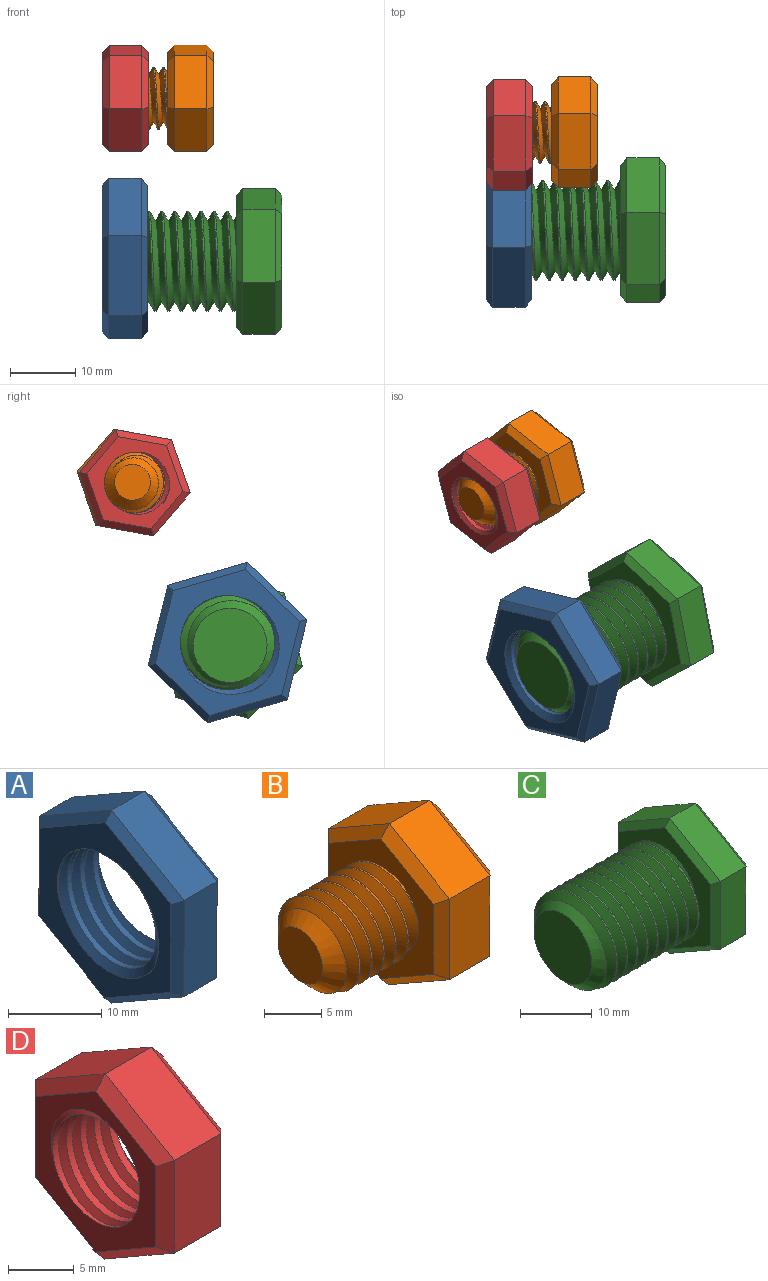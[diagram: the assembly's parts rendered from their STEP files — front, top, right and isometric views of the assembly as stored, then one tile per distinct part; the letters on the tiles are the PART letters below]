
ASSEMBLY  parts=4 mates=2
PART A: 23 faces, bbox 9.3x22.7x26 mm
  f0: cylinder r=7.24mm len=14.48mm, axis (1,0,0), area 111.6mm2, adj f7,f8,f21,f22
  f1: plane 10.98x6.38mm, normal (0,-0.5,0.86), area 63.5mm2, adj f2,f6,f14,f18
  f2: plane 12.7x5mm, normal (0,-1,0), area 63.5mm2, adj f1,f3,f12,f16
  f3: plane 11.02x6.32mm, normal (0,-0.5,-0.87), area 63.5mm2, adj f2,f4,f10,f15
  f4: plane 10.98x6.38mm, normal (0,0.5,-0.86), area 63.5mm2, adj f3,f5,f9,f17
  f5: plane 12.7x5mm, normal (0,1,0), area 63.5mm2, adj f4,f6,f11,f19
  f6: plane 11.02x6.32mm, normal (0,0.5,0.87), area 63.5mm2, adj f1,f5,f13,f20
  f7: plane 23.73x20.67mm, normal (-1,0,0), area 164.4mm2, adj f0,f9,f10,f11,f12,f13,f14,f21
  f8: plane 23.73x20.67mm, normal (1,0,0), area 164.4mm2, adj f0,f15,f16,f17,f18,f19,f20,f21
  f9: plane 10.99x6.96mm, normal (-0.71,0.36,-0.61), area 17.1mm2, adj f4,f7,f10,f11
  f10: plane 11.02x6.9mm, normal (-0.71,-0.35,-0.61), area 17.1mm2, adj f3,f7,f9,f12
  f11: plane 12.7x1.03mm, normal (-0.71,0.71,0), area 17.1mm2, adj f5,f7,f9,f13
  f12: plane 12.7x1.03mm, normal (-0.71,-0.71,0), area 17.1mm2, adj f2,f7,f10,f14
  f13: plane 11.02x6.9mm, normal (-0.71,0.35,0.61), area 17.1mm2, adj f6,f7,f11,f14
  f14: plane 10.99x6.96mm, normal (-0.71,-0.36,0.61), area 17.1mm2, adj f1,f7,f12,f13
  f15: plane 11.02x6.9mm, normal (0.71,-0.35,-0.61), area 17.1mm2, adj f3,f8,f16,f17
  f16: plane 12.7x1.03mm, normal (0.71,-0.71,0), area 17.1mm2, adj f2,f8,f15,f18
  f17: plane 10.99x6.96mm, normal (0.71,0.36,-0.61), area 17.1mm2, adj f4,f8,f15,f19
  f18: plane 10.99x6.96mm, normal (0.71,-0.36,0.61), area 17.1mm2, adj f1,f8,f16,f20
  f19: plane 12.7x1.03mm, normal (0.71,0.71,0), area 17.1mm2, adj f5,f8,f17,f20
  f20: plane 11.02x6.9mm, normal (0.71,0.35,0.61), area 17.1mm2, adj f6,f8,f18,f19
  f21: bspline ~19.31x16.73mm, area 223mm2, adj f0,f7,f8,f22
  f22: bspline ~19.31x16.73mm, area 223mm2, adj f0,f7,f8,f21
PART B: 25 faces, bbox 17.8x15.9x18.1 mm
  f0: cylinder r=4.75mm len=9.5mm, axis (1,0,0), area 28.1mm2, adj f1,f2,f4,f12
  f1: bspline ~10.97x9.91mm, area 196.7mm2, adj f0,f2,f4,f12
  f2: bspline ~10.97x10.66mm, area 196.6mm2, adj f0,f1,f4,f12
  f3: plane 5.5x5.5mm, normal (-1,0,0), area 23.8mm2, adj f4
  f4: cone r=4.75mm half-angle=45deg, axis (1,0,0), area 47.4mm2, adj f0,f1,f2,f3
  f5: plane 7.48x5mm, normal (0,-0.5,0.86), area 43.3mm2, adj f6,f10,f18,f22
  f6: plane 8.66x5mm, normal (0,-1,0), area 43.3mm2, adj f5,f7,f16,f20
  f7: plane 7.52x5mm, normal (0,-0.5,-0.87), area 43.3mm2, adj f6,f8,f14,f19
  f8: plane 7.48x5mm, normal (0,0.5,-0.86), area 43.3mm2, adj f7,f9,f13,f21
  f9: plane 8.66x5mm, normal (0,1,0), area 43.3mm2, adj f8,f10,f15,f23
  f10: plane 7.52x5mm, normal (0,0.5,0.87), area 43.3mm2, adj f5,f9,f17,f24
  f11: plane 15.01x13.03mm, normal (1,0,0), area 146.4mm2, adj f13,f14,f15,f16,f17,f18
  f12: plane 15.83x13.85mm, normal (-1,0,0), area 89.2mm2, adj f0,f1,f2,f19,f20,f21,f22,f23
  f13: plane 7.49x4.93mm, normal (0.71,0.36,-0.61), area 11.4mm2, adj f8,f11,f14,f15
  f14: plane 7.52x4.88mm, normal (0.71,-0.35,-0.61), area 11.4mm2, adj f7,f11,f13,f16
  f15: plane 8.66x1.03mm, normal (0.71,0.71,0), area 11.4mm2, adj f9,f11,f13,f17
  f16: plane 8.66x1.03mm, normal (0.71,-0.71,0), area 11.4mm2, adj f6,f11,f14,f18
  f17: plane 7.52x4.88mm, normal (0.71,0.35,0.61), area 11.4mm2, adj f10,f11,f15,f18
  f18: plane 7.49x4.93mm, normal (0.71,-0.36,0.61), area 11.4mm2, adj f5,f11,f16,f17
  f19: plane 7.52x4.88mm, normal (-0.71,-0.35,-0.61), area 11.4mm2, adj f7,f12,f20,f21
  f20: plane 8.66x1.03mm, normal (-0.71,-0.71,0), area 11.4mm2, adj f6,f12,f19,f22
  f21: plane 7.49x4.93mm, normal (-0.71,0.36,-0.61), area 11.4mm2, adj f8,f12,f19,f23
  f22: plane 7.49x4.93mm, normal (-0.71,-0.36,0.61), area 11.4mm2, adj f5,f12,f20,f24
  f23: plane 8.66x1.03mm, normal (-0.71,0.71,0), area 11.4mm2, adj f9,f12,f21,f24
  f24: plane 7.52x4.88mm, normal (-0.71,0.35,0.61), area 11.4mm2, adj f10,f12,f22,f23
PART C: 26 faces, bbox 27.7x20x23.1 mm
  f0: cylinder r=7.68mm len=18mm, axis (1,0,0), area 139.1mm2, adj f1,f2,f5,f13
  f1: bspline ~20.88x17.74mm, area 713.8mm2, adj f0,f2,f4,f5,f13
  f2: bspline ~21.88x17.74mm, area 715.1mm2, adj f0,f1,f4,f5,f13
  f3: plane 11.36x11.36mm, normal (-1,0,0), area 101.4mm2, adj f4
  f4: cone r=7.68mm half-angle=45deg, axis (1,0,0), area 63.2mm2, adj f1,f2,f3,f5
  f5: cone r=7.68mm half-angle=45deg, axis (1,0,0), area 13.2mm2, adj f0,f1,f2,f4
  f6: plane 9.98x5.81mm, normal (0,-0.5,0.86), area 57.7mm2, adj f7,f11,f19,f23
  f7: plane 11.55x5mm, normal (0,-1,0), area 57.7mm2, adj f6,f8,f17,f21
  f8: plane 10.02x5.74mm, normal (0,-0.5,-0.87), area 57.7mm2, adj f7,f9,f15,f20
  f9: plane 9.98x5.81mm, normal (0,0.5,-0.86), area 57.7mm2, adj f8,f10,f14,f22
  f10: plane 11.55x5mm, normal (0,1,0), area 57.7mm2, adj f9,f11,f16,f24
  f11: plane 10.02x5.74mm, normal (0,0.5,0.87), area 57.7mm2, adj f6,f10,f18,f25
  f12: plane 20.78x18.04mm, normal (1,0,0), area 280.6mm2, adj f14,f15,f16,f17,f18,f19
  f13: plane 20.78x18.04mm, normal (-1,0,0), area 125.2mm2, adj f0,f1,f2,f20,f21,f22,f23,f24
  f14: plane 9.98x6.38mm, normal (0.71,0.36,-0.61), area 15.5mm2, adj f9,f12,f15,f16
  f15: plane 10.02x6.32mm, normal (0.71,-0.35,-0.61), area 15.5mm2, adj f8,f12,f14,f17
  f16: plane 11.55x1.04mm, normal (0.71,0.71,0), area 15.5mm2, adj f10,f12,f14,f18
  f17: plane 11.55x1.04mm, normal (0.71,-0.71,0), area 15.5mm2, adj f7,f12,f15,f19
  f18: plane 10.02x6.32mm, normal (0.71,0.35,0.61), area 15.5mm2, adj f11,f12,f16,f19
  f19: plane 9.98x6.38mm, normal (0.71,-0.36,0.61), area 15.5mm2, adj f6,f12,f17,f18
  f20: plane 10.02x6.32mm, normal (-0.71,-0.35,-0.61), area 15.5mm2, adj f8,f13,f21,f22
  f21: plane 11.55x1.04mm, normal (-0.71,-0.71,0), area 15.5mm2, adj f7,f13,f20,f23
  f22: plane 9.98x6.38mm, normal (-0.71,0.36,-0.61), area 15.5mm2, adj f9,f13,f20,f24
  f23: plane 9.98x6.38mm, normal (-0.71,-0.36,0.61), area 15.5mm2, adj f6,f13,f21,f25
  f24: plane 11.55x1.04mm, normal (-0.71,0.71,0), area 15.5mm2, adj f10,f13,f22,f25
  f25: plane 10.02x6.32mm, normal (-0.71,0.35,0.61), area 15.5mm2, adj f11,f13,f23,f24
PART D: 23 faces, bbox 9.1x15.4x17.7 mm
  f0: plane 7.49x5mm, normal (0,-0.5,0.86), area 43.3mm2, adj f1,f5,f13,f17
  f1: plane 8.66x5mm, normal (0,-1,0), area 43.3mm2, adj f0,f2,f11,f15
  f2: plane 7.51x5mm, normal (0,-0.5,-0.87), area 43.3mm2, adj f1,f3,f9,f14
  f3: plane 7.49x5mm, normal (0,0.5,-0.86), area 43.3mm2, adj f2,f4,f8,f16
  f4: plane 8.66x5mm, normal (0,1,0), area 43.3mm2, adj f3,f5,f10,f18
  f5: plane 7.51x5mm, normal (0,0.5,0.87), area 43.3mm2, adj f0,f4,f12,f19
  f6: plane 15.37x13.38mm, normal (-1,0,0), area 71.4mm2, adj f8,f9,f10,f11,f12,f13,f20,f21
  f7: plane 15.37x13.38mm, normal (1,0,0), area 71.4mm2, adj f14,f15,f16,f17,f18,f19,f20,f21
  f8: plane 7.49x4.93mm, normal (-0.71,0.36,-0.61), area 11.4mm2, adj f3,f6,f9,f10
  f9: plane 7.51x4.89mm, normal (-0.71,-0.35,-0.61), area 11.4mm2, adj f2,f6,f8,f11
  f10: plane 8.66x1.02mm, normal (-0.71,0.71,0), area 11.4mm2, adj f4,f6,f8,f12
  f11: plane 8.66x1.02mm, normal (-0.71,-0.71,0), area 11.4mm2, adj f1,f6,f9,f13
  f12: plane 7.51x4.89mm, normal (-0.71,0.35,0.61), area 11.4mm2, adj f5,f6,f10,f13
  f13: plane 7.49x4.93mm, normal (-0.71,-0.36,0.61), area 11.4mm2, adj f0,f6,f11,f12
  f14: plane 7.51x4.89mm, normal (0.71,-0.35,-0.61), area 11.4mm2, adj f2,f7,f15,f16
  f15: plane 8.66x1.02mm, normal (0.71,-0.71,0), area 11.4mm2, adj f1,f7,f14,f17
  f16: plane 7.49x4.93mm, normal (0.71,0.36,-0.61), area 11.4mm2, adj f3,f7,f14,f18
  f17: plane 7.49x4.93mm, normal (0.71,-0.36,0.61), area 11.4mm2, adj f0,f7,f15,f19
  f18: plane 8.66x1.02mm, normal (0.71,0.71,0), area 11.4mm2, adj f4,f7,f16,f19
  f19: plane 7.51x4.89mm, normal (0.71,0.35,0.61), area 11.4mm2, adj f5,f7,f17,f18
  f20: cylinder r=4.66mm len=9.32mm, axis (1,0,0), area 85.4mm2, adj f6,f7,f21,f22
  f21: bspline ~12.5x10.82mm, area 128.4mm2, adj f6,f7,f20,f22
  f22: bspline ~12.5x10.82mm, area 128.5mm2, adj f6,f7,f20,f21
PLACE A rot(axis=(0,0.6,-0.8),180deg) t=(-55.27,-6.86,23.48)mm fixed
PLACE B rot(axis=(1,0,0),100.4deg) t=(-41.67,7.73,48.08)mm
PLACE C rot(axis=(-1,0,0),14deg) t=(-31.16,-7.25,23.06)mm
PLACE D rot(axis=(1,0,0),100.2deg) t=(-48.16,7.38,48.02)mm fixed
MATE cylindrical C.f0 <-> A.f7  axis (-1,0,0) through (-54.66,-7.25,23.06)mm
MATE cylindrical B.f0 <-> D.f6  axis (-1,0,0) through (-55.17,7.73,48.08)mm
